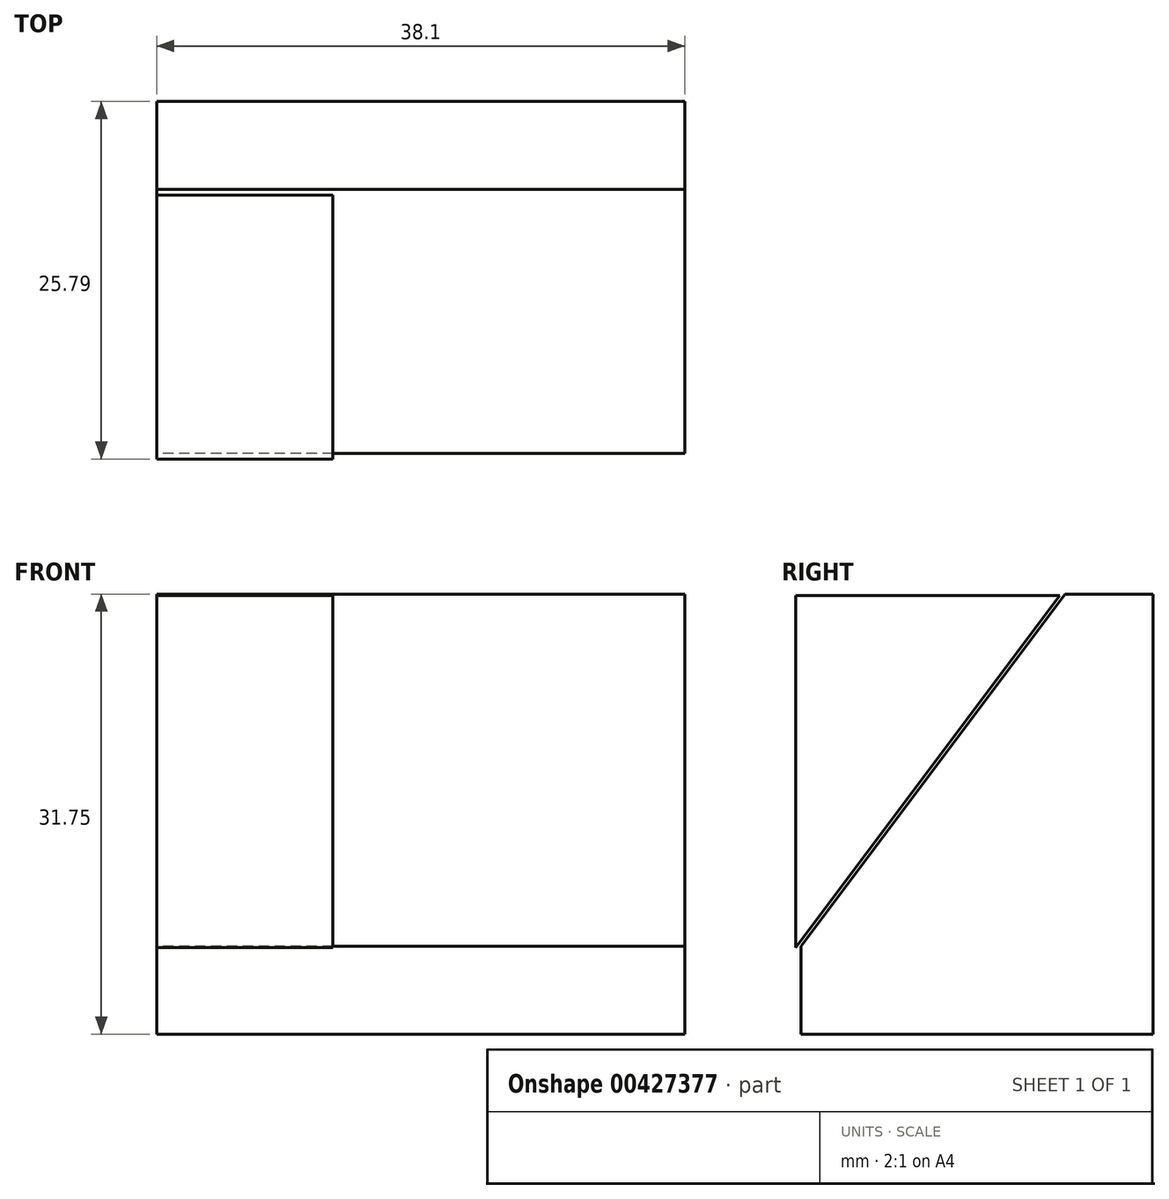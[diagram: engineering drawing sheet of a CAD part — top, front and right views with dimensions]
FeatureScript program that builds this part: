
annotation { "Feature Type Name" : "Feature", "Feature Type Description" : "" }
export const myFeature = defineFeature(function(context is Context, id is Id, definition is map)
    precondition{}
    {
        {
            var Q0;
            Q0=qCreatedBy(makeId("Right.planeOp"),FACE);
            var sketch = newSketch(context, id + "F0", { "sketchPlane" : qUnion([Q0])});
            skLineSegment(sketch, "E0", {"start": v(0, 0) * mm, "end": v(25.4, 0) * mm});
            skLineSegment(sketch, "E1", {"start": v(25.4, 0) * mm, "end": v(25.4, 31.75) * mm});
            skLineSegment(sketch, "E2", {"start": v(25.4, 31.75) * mm, "end": v(19.05, 31.75) * mm});
            skLineSegment(sketch, "E3", {"start": v(0, 0) * mm, "end": v(0, 6.35) * mm});
            skLineSegment(sketch, "E4", {"start": v(0, 6.35) * mm, "end": v(19.05, 31.75) * mm});
            skLineSegment(sketch, "E5", {"start": v(0, 6.35) * mm, "end": v(0, 31.75) * mm});
            skPoint(sketch, "E5.endSnap0", {"position": v(22.23, 31.75) * mm});
            skLineSegment(sketch, "E6", {"start": v(0, 31.75) * mm, "end": v(19.05, 31.75) * mm});
            skSolve(sketch);
        }
        {
            var Q0;
            Q0=makeQuery(id+"F0.imprint","IMPRINT",FACE,{"disambiguationData":[TD([[makeQuery(id+"F0.imprint","IMPRINT",EDGE,{"derivedFrom":sQuery(id+"F0.wireOp",EDGE,"E0")}),1.0]])]});
            extrude(context, id + "F1", {"entities" : qUnion([Q0]), "depth" : 25.4 * mm});
        }
        {
            var Q0;
            Q0=qCreatedBy(makeId("Right.planeOp"),FACE);
            var sketch = newSketch(context, id + "F2", { "sketchPlane" : qUnion([Q0])});
            skLineSegment(sketch, "E7", {"start": v(-0.39, 6.23) * mm, "end": v(-0.39, 31.63) * mm});
            skLineSegment(sketch, "E8", {"start": v(-0.39, 31.63) * mm, "end": v(18.66, 31.63) * mm});
            skLineSegment(sketch, "E9", {"start": v(-0.39, 6.23) * mm, "end": v(18.66, 31.63) * mm});
            skSolve(sketch);
        }
        {
            var Q0;
            Q0=makeQuery(id+"F2.imprint","IMPRINT",FACE,{"disambiguationData":[TD([[makeQuery(id+"F2.imprint","IMPRINT",EDGE,{"derivedFrom":sQuery(id+"F2.wireOp",EDGE,"E7")}),-1.0]])]});
            extrude(context, id + "F3", {"entities" : qUnion([Q0]), "depth" : 12.7 * mm});
        }
        {
            var Q0;
            Q0=makeQuery(id+"F1.opExtrude","CAP_FACE",FACE,{"disambiguationData":[OSD([sQuery(id+"F0.wireOp",EDGE,"E0"),sQuery(id+"F0.wireOp",EDGE,"E1"),sQuery(id+"F0.wireOp",EDGE,"E2"),sQuery(id+"F0.wireOp",EDGE,"E3"),sQuery(id+"F0.wireOp",EDGE,"E4")])],"isStart":false});
            extrude(context, id + "F4", {"entities" : qUnion([Q0]), "operationType" : NewBodyOperationType.ADD, "depth" : 12.7 * mm});
        }
    });
